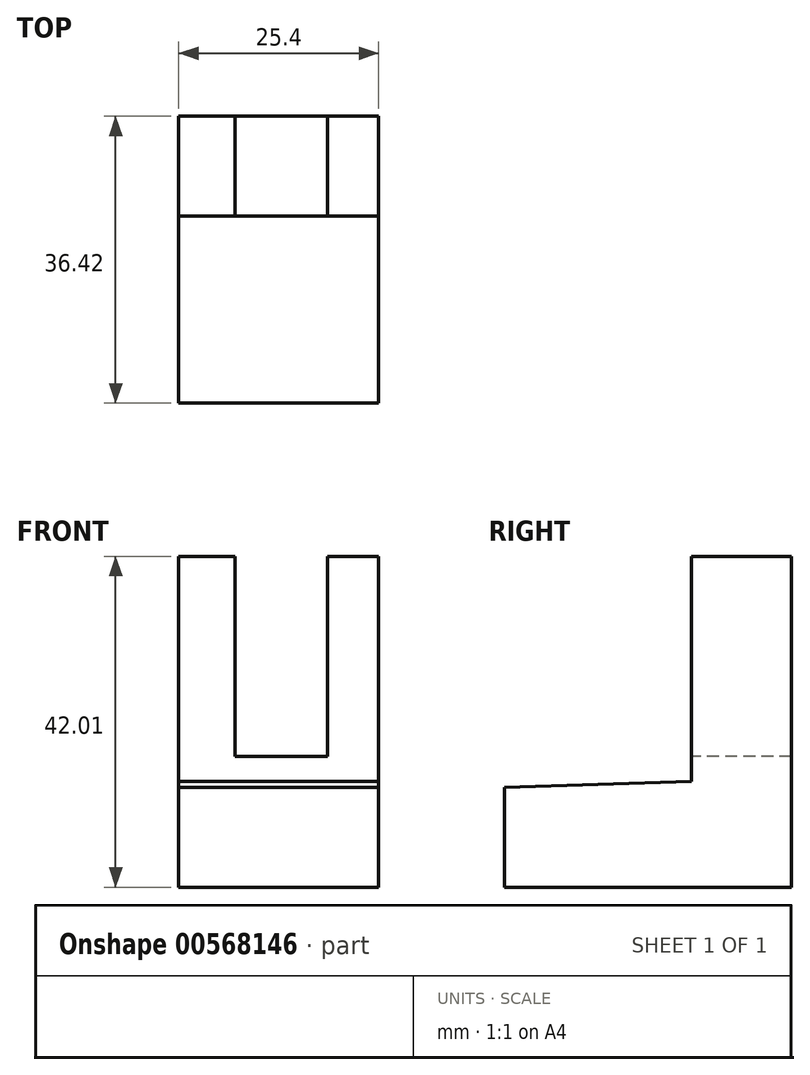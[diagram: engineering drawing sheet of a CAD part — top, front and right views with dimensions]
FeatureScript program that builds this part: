
annotation { "Feature Type Name" : "Feature", "Feature Type Description" : "" }
export const myFeature = defineFeature(function(context is Context, id is Id, definition is map)
    precondition{}
    {
        {
            var Q0;
            Q0=qCreatedBy(makeId("Right.planeOp"),FACE);
            var sketch = newSketch(context, id + "F0", { "sketchPlane" : qUnion([Q0])});
            skLineSegment(sketch, "E0", {"start": v(-33.17, 54.44) * mm, "end": v(-33.17, 25.9) * mm});
            skLineSegment(sketch, "E1", {"start": v(-33.17, 54.44) * mm, "end": v(-20.47, 54.44) * mm});
            skLineSegment(sketch, "E2", {"start": v(-20.47, 54.44) * mm, "end": v(-20.47, 12.43) * mm});
            skLineSegment(sketch, "E3", {"start": v(-20.47, 12.43) * mm, "end": v(-56.9, 12.43) * mm});
            skLineSegment(sketch, "E4", {"start": v(-56.9, 12.43) * mm, "end": v(-56.9, 25.13) * mm});
            skLineSegment(sketch, "E5", {"start": v(-56.9, 25.13) * mm, "end": v(-33.17, 25.9) * mm});
            skSolve(sketch);
        }
        {
            var Q0;
            Q0=makeQuery(id+"F0.imprint","IMPRINT",FACE,{"disambiguationData":[TD([[makeQuery(id+"F0.imprint","IMPRINT",EDGE,{"derivedFrom":sQuery(id+"F0.wireOp",EDGE,"E0")}),1.0]])]});
            extrude(context, id + "F1", {"entities" : qUnion([Q0]), "depth" : 25.4 * mm, "offsetDistance" : 25.4 * mm});
        }
        {
            var Q0;
            Q0=makeQuery(id+"F1.opExtrude","SWEPT_FACE",FACE,{"disambiguationData":[OSD([sQuery(id+"F0.wireOp",EDGE,"E0")])]});
            var sketch = newSketch(context, id + "F2", { "sketchPlane" : qUnion([Q0])});
            skSolve(sketch);
        }
        {
            var Q0;
            {var subQ0=sQuery(id+"F0.wireOp",EDGE,"E0");Q0=makeQuery(id+"F2.imprint","IMPRINT",FACE,{"disambiguationData":[TD([[makeQuery(id+"F2.imprint","IMPRINT",EDGE,{"derivedFrom":makeQuery(id+"F1.opExtrude","CAP_EDGE",EDGE,{"disambiguationData":[OSD([subQ0])],"isStart":true})}),1.0]])]});}
            var sketch = newSketch(context, id + "F3", { "sketchPlane" : qUnion([Q0])});
            skSolve(sketch);
        }
        {
            var Q0;
            Q0=makeQuery(id+"F1.opExtrude","SWEPT_FACE",FACE,{"disambiguationData":[OSD([sQuery(id+"F0.wireOp",EDGE,"E1")])]});
            var sketch = newSketch(context, id + "F4", { "sketchPlane" : qUnion([Q0])});
            skLineSegment(sketch, "E6.bottom", {"start": v(7.13, -20.47) * mm, "end": v(18.92, -20.47) * mm});
            skLineSegment(sketch, "E6.top", {"start": v(7.13, -33.17) * mm, "end": v(18.92, -33.17) * mm});
            skLineSegment(sketch, "E6.left", {"start": v(7.13, -20.47) * mm, "end": v(7.13, -33.17) * mm});
            skLineSegment(sketch, "E6.right", {"start": v(18.92, -20.47) * mm, "end": v(18.92, -33.17) * mm});
            skSolve(sketch);
        }
        {
            var Q0;
            Q0=makeQuery(id+"F4.imprint","IMPRINT",FACE,{"disambiguationData":[TD([[makeQuery(id+"F4.imprint","IMPRINT",EDGE,{"derivedFrom":sQuery(id+"F4.wireOp",EDGE,"E6.bottom")}),1.0]])]});
            extrude(context, id + "F5", {"entities" : qUnion([Q0]), "operationType" : NewBodyOperationType.REMOVE, "oppositeDirection" : true, "depth" : 25.4 * mm, "offsetDistance" : 25.4 * mm});
        }
    });
